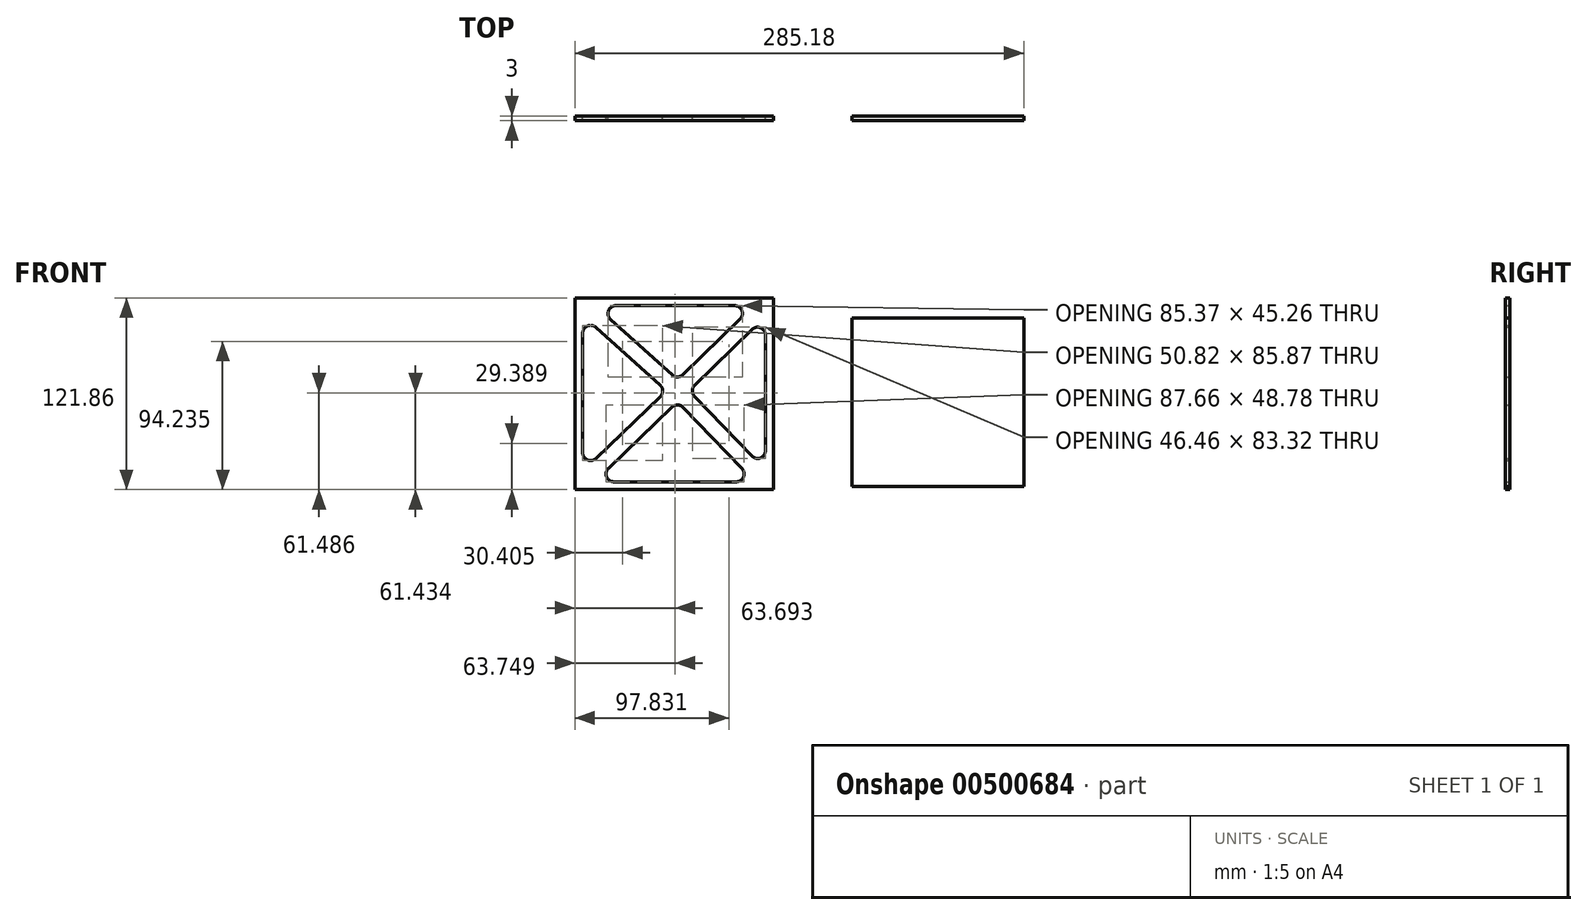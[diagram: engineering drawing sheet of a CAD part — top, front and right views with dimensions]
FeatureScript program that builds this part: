
annotation { "Feature Type Name" : "Feature", "Feature Type Description" : "" }
export const myFeature = defineFeature(function(context is Context, id is Id, definition is map)
    precondition{}
    {
        {
            var Q0;
            Q0=qCreatedBy(makeId("Front.planeOp"),FACE);
            var sketch = newSketch(context, id + "F0", { "sketchPlane" : qUnion([Q0])});
            skLineSegment(sketch, "E0.bottom", {"start": v(-65.5, 58.95) * mm, "end": v(60.56, 58.95) * mm});
            skLineSegment(sketch, "E0.top", {"start": v(-65.5, -62.9) * mm, "end": v(60.56, -62.9) * mm});
            skLineSegment(sketch, "E0.left", {"start": v(-65.5, 58.95) * mm, "end": v(-65.5, -62.9) * mm});
            skLineSegment(sketch, "E0.right", {"start": v(60.56, 58.95) * mm, "end": v(60.56, -62.9) * mm});
            skLineSegment(sketch, "E1.0", {"start": v(-39.44, 53.95) * mm, "end": v(35.95, 53.95) * mm});
            skLineSegment(sketch, "E2.0", {"start": v(55.56, 35.26) * mm, "end": v(55.56, -38.1) * mm});
            skLineSegment(sketch, "E3.0", {"start": v(-40.66, -57.9) * mm, "end": v(37.05, -57.9) * mm});
            skLineSegment(sketch, "E3.1", {"start": v(-60.5, 36.5) * mm, "end": v(-60.5, -39.44) * mm});
            skLineSegment(sketch, "E4", {"start": v(0, 0) * mm, "end": v(60.56, 58.95) * mm});
            skLineSegment(sketch, "E5", {"start": v(-65.5, -62.9) * mm, "end": v(0, 0) * mm});
            skLineSegment(sketch, "E6", {"start": v(-65.5, 58.95) * mm, "end": v(0, 0) * mm});
            skLineSegment(sketch, "E7", {"start": v(60.56, -62.9) * mm, "end": v(0, 0) * mm});
            skLineSegment(sketch, "E8.0", {"start": v(3.22, 10.11) * mm, "end": v(39.44, 45.37) * mm});
            skLineSegment(sketch, "E9.0", {"start": v(10.61, 3.35) * mm, "end": v(47.07, 38.85) * mm});
            skLineSegment(sketch, "E10.0", {"start": v(-44.12, -49.3) * mm, "end": v(-3.74, -10.52) * mm});
            skLineSegment(sketch, "E11.0", {"start": v(-52.04, -43.05) * mm, "end": v(-11.22, -3.84) * mm});
            skLineSegment(sketch, "E12.0", {"start": v(-52.16, 40.22) * mm, "end": v(-11.34, 3.48) * mm});
            skLineSegment(sketch, "E13.0", {"start": v(-42.79, 45.24) * mm, "end": v(-3.61, 9.98) * mm});
            skArc(sketch, "E14.filletArc", {"start": v(-52.16, 40.22) * mm, "mid": v(-57.54, 41.07) * mm, "end": v(-60.5, 36.5) * mm});
            skArc(sketch, "E15.filletArc", {"start": v(-11.22, -3.84) * mm, "mid": v(-9.68, -0.16) * mm, "end": v(-11.34, 3.48) * mm});
            skArc(sketch, "E16.filletArc", {"start": v(-60.5, -39.44) * mm, "mid": v(-57.46, -44.04) * mm, "end": v(-52.04, -43.05) * mm});
            skArc(sketch, "E17.filletArc", {"start": v(-44.12, -49.3) * mm, "mid": v(-45.3, -54.78) * mm, "end": v(-40.66, -57.9) * mm});
            skLineSegment(sketch, "E18.0", {"start": v(46.96, -41.57) * mm, "end": v(10.5, -3.7) * mm});
            skLineSegment(sketch, "E19.0", {"start": v(40.66, -49.44) * mm, "end": v(3.32, -10.66) * mm});
            skArc(sketch, "E20.filletArc", {"start": v(3.32, -10.66) * mm, "mid": v(-0.18, -9.13) * mm, "end": v(-3.74, -10.52) * mm});
            skArc(sketch, "E21.filletArc", {"start": v(37.05, -57.9) * mm, "mid": v(41.65, -54.87) * mm, "end": v(40.66, -49.44) * mm});
            skArc(sketch, "E22.filletArc", {"start": v(46.96, -41.57) * mm, "mid": v(52.43, -42.74) * mm, "end": v(55.56, -38.1) * mm});
            skArc(sketch, "E23.filletArc", {"start": v(10.61, 3.35) * mm, "mid": v(9.1, -0.15) * mm, "end": v(10.5, -3.7) * mm});
            skArc(sketch, "E24.filletArc", {"start": v(-39.44, 53.95) * mm, "mid": v(-44.11, 50.75) * mm, "end": v(-42.79, 45.24) * mm});
            skArc(sketch, "E25.filletArc", {"start": v(-3.61, 9.98) * mm, "mid": v(-0.17, 8.7) * mm, "end": v(3.22, 10.11) * mm});
            skArc(sketch, "E26.filletArc", {"start": v(55.56, 35.26) * mm, "mid": v(52.5, 39.87) * mm, "end": v(47.07, 38.85) * mm});
            skArc(sketch, "E27.filletArc", {"start": v(39.44, 45.37) * mm, "mid": v(40.58, 50.84) * mm, "end": v(35.95, 53.95) * mm});
            skSolve(sketch);
        }
        {
            var Q0;
            Q0=makeQuery(id+"F0.imprint","IMPRINT",FACE,{"disambiguationData":[TD([[makeQuery(id+"F0.imprint","IMPRINT",EDGE,{"derivedFrom":sQuery(id+"F0.wireOp",EDGE,"E0.bottom")}),-1.0]])]});
            var Q1;
            Q1=makeQuery(id+"F0.imprint","IMPRINT",FACE,{"disambiguationData":[TD([[makeQuery(id+"F0.imprint","IMPRINT",EDGE,{"derivedFrom":sQuery(id+"F0.wireOp",EDGE,"E0.left")}),1.0]])]});
            var Q2;
            Q2=makeQuery(id+"F0.imprint","IMPRINT",FACE,{"disambiguationData":[TD([[makeQuery(id+"F0.imprint","IMPRINT",EDGE,{"derivedFrom":sQuery(id+"F0.wireOp",EDGE,"E0.top")}),1.0]])]});
            var Q3;
            Q3=makeQuery(id+"F0.imprint","IMPRINT",FACE,{"disambiguationData":[TD([[makeQuery(id+"F0.imprint","IMPRINT",EDGE,{"derivedFrom":sQuery(id+"F0.wireOp",EDGE,"E0.right")}),-1.0]])]});
            extrude(context, id + "F1", {"entities" : qUnion([Q0, Q1, Q2, Q3]), "depth" : 3 * mm, "offsetDistance" : 25 * mm});
        }
        {
            var Q0;
            Q0=qCreatedBy(makeId("Front.planeOp"),FACE);
            var sketch = newSketch(context, id + "F2", { "sketchPlane" : qUnion([Q0])});
            skLineSegment(sketch, "E28.bottom", {"start": v(110.51, 46.01) * mm, "end": v(219.68, 46.01) * mm});
            skLineSegment(sketch, "E28.top", {"start": v(110.51, -60.88) * mm, "end": v(219.68, -60.88) * mm});
            skLineSegment(sketch, "E28.left", {"start": v(110.51, 46.01) * mm, "end": v(110.51, -60.88) * mm});
            skLineSegment(sketch, "E28.right", {"start": v(219.68, 46.01) * mm, "end": v(219.68, -60.88) * mm});
            skSolve(sketch);
        }
        {
            var Q0;
            Q0 = qSketchRegion(id + "F2", true);
            extrude(context, id + "F3", {"entities" : qUnion([Q0]), "depth" : 3 * mm, "offsetDistance" : 25 * mm});
        }
    });
